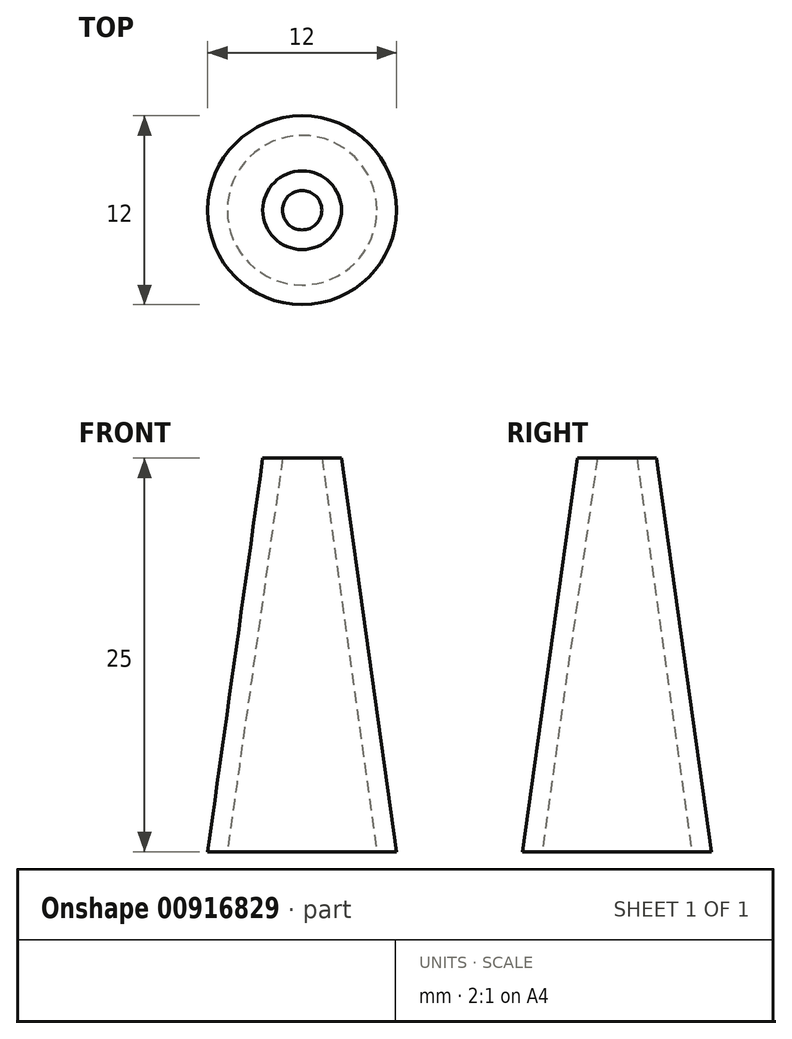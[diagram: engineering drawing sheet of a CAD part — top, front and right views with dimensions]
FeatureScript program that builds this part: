
annotation { "Feature Type Name" : "Feature", "Feature Type Description" : "" }
export const myFeature = defineFeature(function(context is Context, id is Id, definition is map)
    precondition{}
    {
        {
            var Q0;
            Q0=qCreatedBy(makeId("Front.planeOp"),FACE);
            var sketch = newSketch(context, id + "F0", { "sketchPlane" : qUnion([Q0])});
            skLineSegment(sketch, "E0", {"start": v(0, 0) * mm, "end": v(1.25, 0) * mm});
            skLineSegment(sketch, "E1", {"start": v(-4.75, 0) * mm, "end": v(-4.75, 25) * mm});
            skLineSegment(sketch, "E2", {"start": v(1.25, 0) * mm, "end": v(-2.25, 25) * mm});
            skLineSegment(sketch, "E3", {"start": v(0, 0) * mm, "end": v(-3.5, 25) * mm});
            skLineSegment(sketch, "E4", {"start": v(-3.5, 25) * mm, "end": v(-2.25, 25) * mm});
            skSolve(sketch);
        }
        {
            var Q0;
            Q0 = qSketchRegion(id + "F0", true);
            var Q1;
            Q1=sQuery(id+"F0.wireOp",EDGE,"E1");
            revolve(context, id + "F1", {"surfaceOperationType" : NewSurfaceOperationType.NEW, "entities" : qUnion([Q0]), "axis" : qUnion([Q1]), "revolveType" : RevolveType.FULL});
        }
    });
